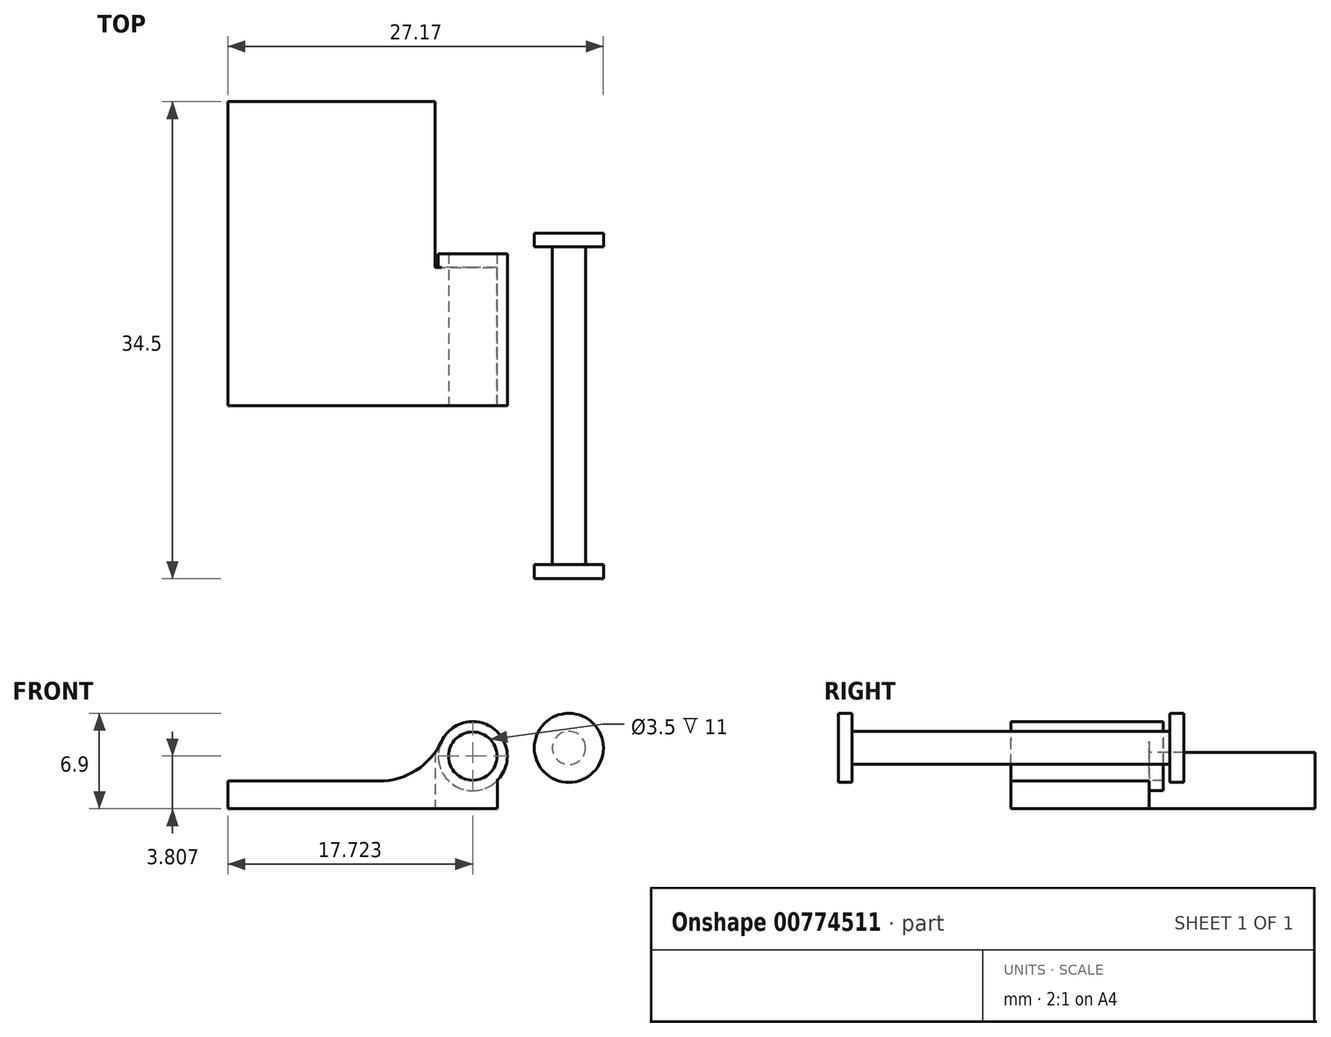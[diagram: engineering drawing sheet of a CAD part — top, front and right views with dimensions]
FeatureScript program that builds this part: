
annotation { "Feature Type Name" : "Feature", "Feature Type Description" : "" }
export const myFeature = defineFeature(function(context is Context, id is Id, definition is map)
    precondition{}
    {
        {
            var Q0;
            Q0=qCreatedBy(makeId("Top.planeOp"),FACE);
            var sketch = newSketch(context, id + "F0", { "sketchPlane" : qUnion([Q0])});
            skLineSegment(sketch, "E0.bottom", {"start": v(0, 0) * mm, "end": v(-15, 0) * mm});
            skLineSegment(sketch, "E0.top", {"start": v(0, 22) * mm, "end": v(-15, 22) * mm});
            skLineSegment(sketch, "E0.left", {"start": v(0, 0) * mm, "end": v(0, 22) * mm});
            skLineSegment(sketch, "E0.right", {"start": v(-15, 0) * mm, "end": v(-15, 22) * mm});
            skLineSegment(sketch, "E1.bottom", {"start": v(0, 0) * mm, "end": v(4.5, 0) * mm});
            skLineSegment(sketch, "E1.top", {"start": v(0, 10) * mm, "end": v(4.5, 10) * mm});
            skLineSegment(sketch, "E1.left", {"start": v(0, 0) * mm, "end": v(0, 10) * mm});
            skLineSegment(sketch, "E1.right", {"start": v(4.5, 0) * mm, "end": v(4.5, 10) * mm});
            skSolve(sketch);
        }
        {
            var Q0;
            Q0 = qSketchRegion(id + "F0", true);
            extrude(context, id + "F1", {"entities" : qUnion([Q0]), "depth" : 2 * mm, "offsetDistance" : 25 * mm});
        }
        {
            var Q0;
            Q0=qCreatedBy(makeId("Front.planeOp"),FACE);
            var sketch = newSketch(context, id + "F2", { "sketchPlane" : qUnion([Q0])});
            skCircle(sketch, "E2", {"center": v(2.72, 3.8) * mm, "radius": 2.5 * mm});
            skCircle(sketch, "E3", {"center": v(2.72, 3.8) * mm, "radius": 1.75 * mm});
            skSolve(sketch);
        }
        {
            var Q0;
            Q0=makeQuery(id+"F2.imprint","IMPRINT",FACE,{"disambiguationData":[TD([[makeQuery(id+"F2.imprint","IMPRINT",EDGE,{"derivedFrom":sQuery(id+"F2.wireOp",EDGE,"E2")}),1.0]])]});
            extrude(context, id + "F3", {"entities" : qUnion([Q0]), "operationType" : NewBodyOperationType.ADD, "oppositeDirection" : true, "depth" : 11 * mm, "offsetDistance" : 25 * mm});
        }
        {
            var Q0;
            Q0=makeQuery(id+"F3.boolean.opBoolean","INTERSECT",EDGE,{"disambiguationData":[OD(0.0)],"derivedFrom":[makeQuery(id+"F1.opExtrude","CAP_FACE",FACE,{"disambiguationData":[OSD([sQuery(id+"F0.wireOp",EDGE,"E0.bottom"),sQuery(id+"F0.wireOp",EDGE,"E0.top"),sQuery(id+"F0.wireOp",EDGE,"E0.left"),sQuery(id+"F0.wireOp",EDGE,"E0.right"),sQuery(id+"F0.wireOp",EDGE,"E1.bottom"),sQuery(id+"F0.wireOp",EDGE,"E1.top"),sQuery(id+"F0.wireOp",EDGE,"E1.right")])],"isStart":false}),makeQuery(id+"F3.opExtrude","SWEPT_FACE",FACE,{"disambiguationData":[OSD([sQuery(id+"F2.wireOp",EDGE,"E2")])]})]});
            fillet(context, id + "F4", {"entities" : qUnion([Q0]), "radius" : 5 * mm, "tangentPropagation" : true, "allowEdgeOverflow" : false});
        }
        {
            var Q0;
            Q0=qCreatedBy(makeId("Front.planeOp"),FACE);
            var sketch = newSketch(context, id + "F5", { "sketchPlane" : qUnion([Q0])});
            skCircle(sketch, "E4", {"center": v(9.67, 4.4) * mm, "radius": 1.2 * mm});
            skSolve(sketch);
        }
        {
            var Q0;
            Q0 = qSketchRegion(id + "F5", true);
            extrude(context, id + "F6", {"entities" : qUnion([Q0]), "endBound" : BoundingType.SYMMETRIC, "depth" : 23 * mm, "offsetDistance" : 25 * mm});
        }
        {
            var Q0;
            Q0=makeQuery(id+"F6.opExtrude","CAP_FACE",FACE,{"disambiguationData":[OSD([sQuery(id+"F5.wireOp",EDGE,"E4")])],"isStart":true});
            var sketch = newSketch(context, id + "F7", { "sketchPlane" : qUnion([Q0])});
            skCircle(sketch, "E5", {"center": v(-9.67, 4.4) * mm, "radius": 2.5 * mm});
            skSolve(sketch);
        }
        {
            var Q0;
            Q0 = qSketchRegion(id + "F7", true);
            extrude(context, id + "F8", {"entities" : qUnion([Q0]), "operationType" : NewBodyOperationType.ADD, "depth" : 1 * mm, "offsetDistance" : 25 * mm});
        }
        {
            var Q0;
            Q0=makeQuery(id+"F6.opExtrude","CAP_FACE",FACE,{"disambiguationData":[OSD([sQuery(id+"F5.wireOp",EDGE,"E4")])],"isStart":false});
            var sketch = newSketch(context, id + "F9", { "sketchPlane" : qUnion([Q0])});
            skCircle(sketch, "E6", {"center": v(9.67, 4.4) * mm, "radius": 2.5 * mm});
            skSolve(sketch);
        }
        {
            var Q0;
            Q0 = qSketchRegion(id + "F9", true);
            extrude(context, id + "F10", {"entities" : qUnion([Q0]), "operationType" : NewBodyOperationType.ADD, "depth" : 1 * mm, "offsetDistance" : 25 * mm});
        }
    });
